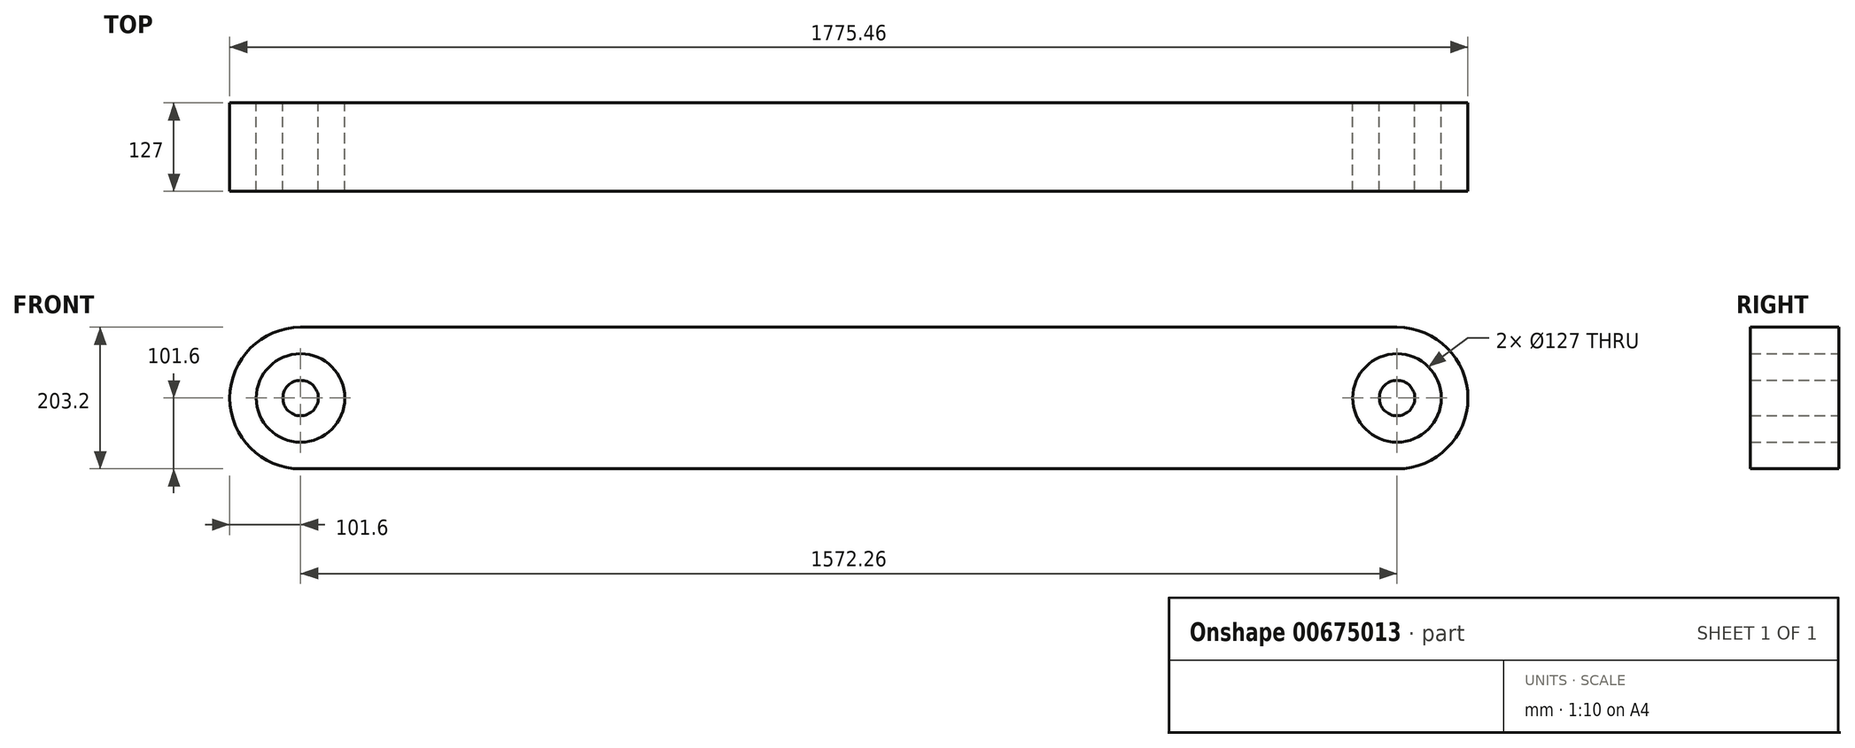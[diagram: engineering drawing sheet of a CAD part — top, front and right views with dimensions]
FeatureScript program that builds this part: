
annotation { "Feature Type Name" : "Feature", "Feature Type Description" : "" }
export const myFeature = defineFeature(function(context is Context, id is Id, definition is map)
    precondition{}
    {
        {
            var Q0;
            Q0=qCreatedBy(makeId("Front.planeOp"),FACE);
            var sketch = newSketch(context, id + "F0", { "sketchPlane" : qUnion([Q0])});
            skLineSegment(sketch, "E0.bottom", {"start": v(0, 0) * mm, "end": v(1572.26, 0) * mm});
            skLineSegment(sketch, "E0.top", {"start": v(0, 203.2) * mm, "end": v(1572.26, 203.2) * mm});
            skArc(sketch, "E1", {"start": v(0, 203.2) * mm, "mid": v(-101.6, 101.6) * mm, "end": v(0, 0) * mm});
            skArc(sketch, "E2", {"start": v(1572.26, 0) * mm, "mid": v(1673.86, 101.6) * mm, "end": v(1572.26, 203.2) * mm});
            skCircle(sketch, "E3", {"center": v(0, 101.6) * mm, "radius": 63.5 * mm});
            skCircle(sketch, "E4", {"center": v(0, 101.6) * mm, "radius": 25.4 * mm});
            skCircle(sketch, "E5", {"center": v(1572.26, 101.6) * mm, "radius": 63.5 * mm});
            skCircle(sketch, "E6", {"center": v(1572.26, 101.6) * mm, "radius": 25.4 * mm});
            skSolve(sketch);
        }
        {
            var Q0;
            Q0=makeQuery(id+"F0.imprint","IMPRINT",FACE,{"disambiguationData":[TD([[makeQuery(id+"F0.imprint","IMPRINT",EDGE,{"derivedFrom":sQuery(id+"F0.wireOp",EDGE,"E0.bottom")}),1.0]])]});
            var Q1;
            Q1=makeQuery(id+"F0.imprint","IMPRINT",FACE,{"disambiguationData":[TD([[makeQuery(id+"F0.imprint","IMPRINT",EDGE,{"derivedFrom":sQuery(id+"F0.wireOp",EDGE,"E4")}),1.0]])]});
            var Q2;
            Q2=makeQuery(id+"F0.imprint","IMPRINT",FACE,{"disambiguationData":[TD([[makeQuery(id+"F0.imprint","IMPRINT",EDGE,{"derivedFrom":sQuery(id+"F0.wireOp",EDGE,"E6")}),1.0]])]});
            extrude(context, id + "F1", {"entities" : qUnion([Q0, Q1, Q2]), "depth" : 127 * mm, "offsetDistance" : 25.4 * mm});
        }
    });
